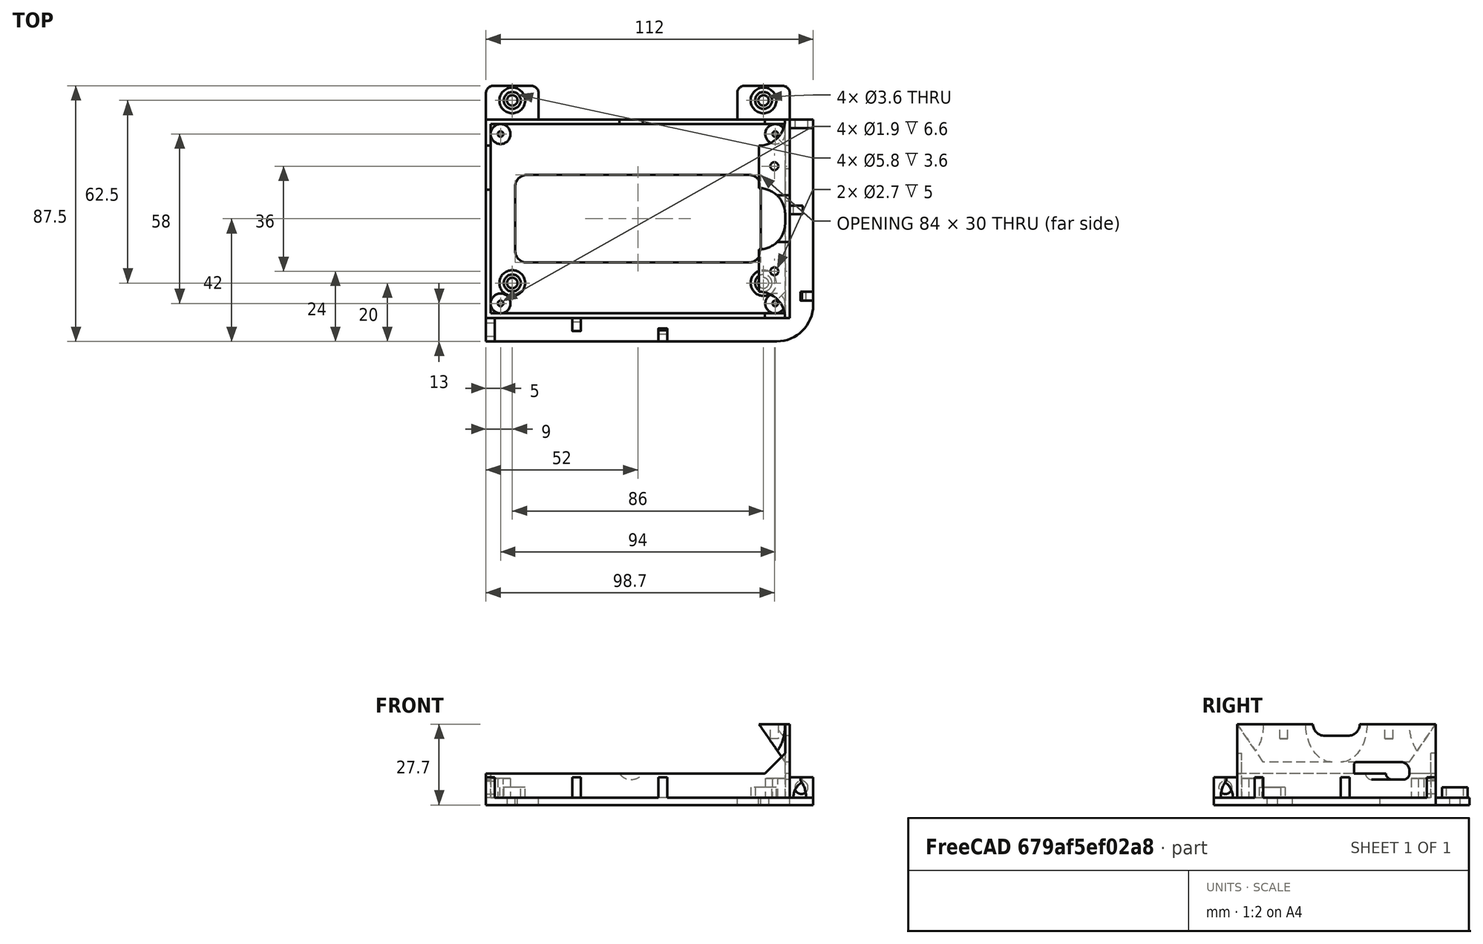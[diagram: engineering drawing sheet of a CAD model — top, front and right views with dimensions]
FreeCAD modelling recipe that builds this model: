
FCSTD DOCUMENT  (FreeCAD 1.0R39319 (Git))
Label: NanoPC-Rail-90
License: All rights reserved
LicenseURL: https://en.wikipedia.org/wiki/All_rights_reserved
objects: Sketcher::SketchObject×22, PartDesign::Pocket×13, PartDesign::Pad×9, App::VarSet×1, PartDesign::Body×1
note: 111 computed .brp shape members not serialized (recipe doc carries the construction recipe); baked Part::Feature solids carry a one-line shape summary decoded from their .brp

FEATURE [App::VarSet] VarSet
  BlackSelfTappingDiameter = 2.7
  Border = 8.2
  DX = 104
  DY = 68
  HoleDX = 94
  HoleDY = 58
  M3HeadDiameter = 5.8
  M3PassThroughDiameter = 3.6
  MiniBlackSelfTappingDiameter = 1.9
  PcbDX = 100.8
  PcbDY = 64.8
  PoleDiameter = 6.8
  PoleHeight = 6.6
  RailScrewDistance = 62.5
  Thickness = 2.5
  TopPcbWallHeight = 17
  WallThickness = 1.6
  expr: DX = PcbDX + 2 * WallThickness
  expr: DY = PcbDY + 2 * WallThickness
FEATURE [Sketcher::SketchObject] Sketch
  ArcFitTolerance = 1e-06
  AttachmentSupport = -> [XY_Plane]
  FullyConstrained = true
  MakeInternals = false
  MapMode = 5
  expr: Constraints[10] = VarSet.DY
  expr: Constraints[55] = VarSet.M3PassThroughDiameter
  expr: Constraints[64] = VarSet.RailScrewDistance
  expr: Constraints[9] = VarSet.DX
  sketch-geometry (46):
    g0: LineSegment StartX=-52 StartY=34 StartZ=0 EndX=-52 EndY=-34 EndZ=0
    g1: LineSegment [constr] StartX=-52 StartY=-34 StartZ=0 EndX=52 EndY=-34 EndZ=0
    g2: LineSegment [constr] StartX=52 StartY=-34 StartZ=0 EndX=52 EndY=34 EndZ=0
    g3: LineSegment [constr] StartX=52 StartY=34 StartZ=0 EndX=-52 EndY=34 EndZ=0
    g4: LineSegment StartX=-52 StartY=-34 StartZ=0 EndX=-52 EndY=-42 EndZ=0
    g5: LineSegment StartX=-52 StartY=-42 StartZ=0 EndX=47.5 EndY=-42 EndZ=0
    g6: LineSegment StartX=52 StartY=34 StartZ=0 EndX=60 EndY=34 EndZ=0
    g7: LineSegment StartX=60 StartY=34 StartZ=0 EndX=60 EndY=-29.5 EndZ=0
    g8: LineSegment StartX=-42 StartY=11 StartZ=0 EndX=-42 EndY=-11 EndZ=0
    g9: LineSegment StartX=-38 StartY=-15 StartZ=0 EndX=38 EndY=-15 EndZ=0
    g10: LineSegment StartX=42 StartY=-11 StartZ=0 EndX=42 EndY=11 EndZ=0
    g11: LineSegment StartX=38 StartY=15 StartZ=0 EndX=-38 EndY=15 EndZ=0
    g12: ArcOfCircle CenterX=-38 CenterY=11 CenterZ=0 NormalX=0 NormalY=0 NormalZ=1 AngleXU=0 Radius=4 StartAngle=1.5708 EndAngle=3.14159
    g13: ArcOfCircle CenterX=-38 CenterY=-11 CenterZ=0 NormalX=0 NormalY=0 NormalZ=1 AngleXU=0 Radius=4 StartAngle=3.14159 EndAngle=4.71239
    g14: ArcOfCircle CenterX=38 CenterY=-11 CenterZ=0 NormalX=0 NormalY=0 NormalZ=1 AngleXU=0 Radius=4 StartAngle=4.71239 EndAngle=6.28319
    g15: ArcOfCircle CenterX=38 CenterY=11 CenterZ=0 NormalX=0 NormalY=0 NormalZ=1 AngleXU=0 Radius=4 StartAngle=0 EndAngle=1.5708
    g16: GeomPoint [constr] X=-42 Y=15 Z=0
    g17: GeomPoint [constr] X=42 Y=-15 Z=0
    g18: LineSegment [constr] StartX=-42 StartY=11 StartZ=0 EndX=-52 EndY=11 EndZ=0
    g19: LineSegment [constr] StartX=-38 StartY=15 StartZ=0 EndX=-38 EndY=34 EndZ=0
    g20: ArcOfCircle CenterX=47.5 CenterY=-29.5 CenterZ=0 NormalX=0 NormalY=0 NormalZ=1 AngleXU=0 Radius=12.5 StartAngle=4.71239 EndAngle=6.28319
    g21: Circle CenterX=-43 CenterY=-22 CenterZ=0 NormalX=0 NormalY=0 NormalZ=1 AngleXU=0 Radius=1.8
    g22: Circle CenterX=43 CenterY=-22 CenterZ=0 NormalX=0 NormalY=0 NormalZ=1 AngleXU=0 Radius=1.8
    g23: LineSegment [constr] StartX=-43 StartY=-22 StartZ=0 EndX=-52 EndY=-22 EndZ=0
    g24: Circle CenterX=-43 CenterY=40.5 CenterZ=0 NormalX=0 NormalY=0 NormalZ=1 AngleXU=0 Radius=1.8
    g25: LineSegment [constr] StartX=-43 StartY=-22 StartZ=0 EndX=-43 EndY=40.5 EndZ=0
    g26: LineSegment [constr] StartX=43 StartY=-22 StartZ=0 EndX=43 EndY=-34 EndZ=0
    g27: LineSegment [constr] StartX=43 StartY=-22 StartZ=0 EndX=43 EndY=40.5 EndZ=0
    g28: Circle CenterX=43 CenterY=40.5 CenterZ=0 NormalX=0 NormalY=0 NormalZ=1 AngleXU=0 Radius=1.8
    g29: LineSegment StartX=-52 StartY=34 StartZ=0 EndX=-52 EndY=43 EndZ=0
    g30: LineSegment StartX=-34 StartY=34 StartZ=0 EndX=-34 EndY=43 EndZ=0
    g31: LineSegment StartX=-49.5 StartY=45.5 StartZ=0 EndX=-36.5 EndY=45.5 EndZ=0
    g32: ArcOfCircle CenterX=-36.5 CenterY=43 CenterZ=0 NormalX=0 NormalY=0 NormalZ=1 AngleXU=0 Radius=2.5 StartAngle=0 EndAngle=1.5708
    g33: ArcOfCircle CenterX=-49.5 CenterY=43 CenterZ=0 NormalX=0 NormalY=0 NormalZ=1 AngleXU=0 Radius=2.5 StartAngle=1.5708 EndAngle=3.14159
    g34: LineSegment [constr] StartX=-52 StartY=34 StartZ=0 EndX=-43 EndY=40.5 EndZ=0
    g35: LineSegment [constr] StartX=-34 StartY=34 StartZ=0 EndX=-43 EndY=40.5 EndZ=0
    g36: LineSegment [constr] StartX=-43 StartY=40.5 StartZ=0 EndX=-43 EndY=45.5 EndZ=0
    g37: LineSegment [constr] StartX=43 StartY=40.5 StartZ=0 EndX=34 EndY=34 EndZ=0
    g38: LineSegment [constr] StartX=43 StartY=40.5 StartZ=0 EndX=52 EndY=34 EndZ=0
    g39: LineSegment StartX=34 StartY=34 StartZ=0 EndX=34 EndY=43 EndZ=0
    g40: LineSegment StartX=52 StartY=34 StartZ=0 EndX=52 EndY=43 EndZ=0
    g41: LineSegment [constr] StartX=43 StartY=40.5 StartZ=0 EndX=43 EndY=45.5 EndZ=0
    g42: LineSegment StartX=36.5 StartY=45.5 StartZ=0 EndX=49.5 EndY=45.5 EndZ=0
    g43: ArcOfCircle CenterX=49.5 CenterY=43 CenterZ=0 NormalX=0 NormalY=0 NormalZ=1 AngleXU=0 Radius=2.5 StartAngle=1e-16 EndAngle=1.5708
    g44: ArcOfCircle CenterX=36.5 CenterY=43 CenterZ=0 NormalX=0 NormalY=0 NormalZ=1 AngleXU=0 Radius=2.5 StartAngle=1.5708 EndAngle=3.14159
    g45: LineSegment StartX=-34 StartY=34 StartZ=0 EndX=34 EndY=34 EndZ=0
  constraints (117):
    c: Coincident(g0,g1)
    c: Coincident(g1,g2)
    c: Coincident(g2,g3)
    c: Coincident(g3,g0)
    c: Vertical(g0)
    c: Vertical(g2)
    c: Horizontal(g1)
    c: Horizontal(g3)
    c: Symmetric(g1,g0,g-1)
    c: Distance(g3) = 104
    c: Distance(g2) = 68
    c: Coincident(g4,g0)
    c: Vertical(g4)
    c: Coincident(g5,g4)
    c: Horizontal(g5)
    c: Coincident(g6,g2)
    c: Horizontal(g6)
    c: Coincident(g7,g6)
    c: Vertical(g7)
    c: Equal(g6,g4)
    c: Distance(g4) = 8
    c: Tangent(g8,g12) = -1.5708
    c: Tangent(g8,g13) = -1.5708
    c: Tangent(g9,g13) = -1.5708
    c: Tangent(g9,g14) = -1.5708
    c: Tangent(g10,g14) = -1.5708
    c: Tangent(g10,g15) = -1.5708
    c: Tangent(g11,g15) = -1.5708
    c: Tangent(g11,g12) = -1.5708
    c: Vertical(g8)
    c: Vertical(g10)
    c: Horizontal(g9)
    c: Horizontal(g11)
    c: Equal(g12,g13)
    c: Equal(g13,g14)
    c: Equal(g14,g15)
    c: PointOnObject(g16,g8)
    c: PointOnObject(g16,g11)
    c: PointOnObject(g17,g9)
    c: PointOnObject(g17,g10)
    c: Diameter(g15) = 8
    c: Symmetric(g16,g17,g-1)
    c: Coincident(g18,g8)
    c: PointOnObject(g18,g0)
    c: Horizontal(g18)
    c: Distance(g18) = 10
    c: Coincident(g19,g11)
    c: PointOnObject(g19,g3)
    c: Vertical(g19)
    c: Distance(g19) = 19
    c: Diameter(g20) = 25
    c: Tangent(g7,g20) = 1.5708
    c: Tangent(g5,g20) = -1.5708
    c: Symmetric(g22,g21,g-2)
    c: Equal(g22,g21)
    c: Diameter(g22) = 3.6
    c: Coincident(g23,g21)
    c: Horizontal(g23)
    c: PointOnObject(g23,g0)
    c: Distance(g23) = 9
    c: Equal(g24,g22)
    c: Coincident(g25,g21)
    c: Vertical(g25)
    c: Coincident(g25,g24)
    c: Distance(g25) = 62.5
    c: Coincident(g26,g22)
    c: Vertical(g26)
    c: PointOnObject(g26,g1)
    c: Coincident(g27,g22)
    c: Vertical(g27)
    c: Equal(g25,g27)
    c: Coincident(g28,g27)
    c: Equal(g22,g28)
    c: Coincident(g29,g0)
    c: Vertical(g29)
    c: PointOnObject(g30,g3)
    c: Vertical(g30)
    c: Horizontal(g31)
    c: Equal(g29,g30)
    c: Tangent(g33,g31) = 1.5708
    c: Tangent(g33,g29) = 1.5708
    c: Coincident(g32,g30)
    c: Equal(g32,g33)
    c: Coincident(g34,g0)
    c: Coincident(g34,g24)
    c: Coincident(g35,g30)
    c: Coincident(g35,g24)
    c: Equal(g34,g35)
    c: Tangent(g32,g31) = 1.5708
    c: Coincident(g36,g24)
    c: Symmetric(g31,g31,g36)
    c: Distance(g36) = 5
    c: Diameter(g32) = 5
    c: Coincident(g37,g27)
    c: PointOnObject(g37,g3)
    c: Equal(g35,g37)
    c: Coincident(g38,g27)
    c: PointOnObject(g38,g3)
    c: Equal(g37,g38)
    c: Coincident(g39,g37)
    c: Vertical(g39)
    c: Coincident(g40,g38)
    c: Vertical(g40)
    c: Coincident(g41,g27)
    c: Vertical(g41)
    c: Equal(g41,g36)
    c: Horizontal(g42)
    c: PointOnObject(g41,g42)
    c: Tangent(g44,g42) = 1.5708
    c: Tangent(g43,g42) = 1.5708
    c: Tangent(g43,g40) = -1.5708
    c: Tangent(g44,g39) = 1.5708
    c: Equal(g32,g44)
    c: Equal(g44,g43)
    c: Coincident(g45,g30)
    c: Coincident(g45,g37)
    c: Distance(g26) = 12
FEATURE [PartDesign::Pad] Pad  label="Base Structure"
  Direction = (0,0,1)
  Length = 2.5
  Length2 = 10
  Profile = -> Sketch
  ReferenceAxis = -> Sketch [N_Axis]
  Refine = true
  Suppressed = false
  Type = 0
  expr: Length = VarSet.Thickness
FEATURE [Sketcher::SketchObject] Sketch002
  ArcFitTolerance = 1e-06
  AttachmentSupport = -> [Pad]
  FullyConstrained = true
  MakeInternals = false
  MapMode = 5
  Placement = pos=(0,0,2.5) rot=(0,0,1;0rad)
  expr: Constraints[10] = VarSet.PcbDX
  expr: Constraints[17] = VarSet.DX
  expr: Constraints[20] = VarSet.DY
  expr: Constraints[9] = VarSet.PcbDY
  sketch-geometry (8):
    g0: LineSegment StartX=-50.4 StartY=32.4 StartZ=0 EndX=-50.4 EndY=-32.4 EndZ=0
    g1: LineSegment StartX=-50.4 StartY=-32.4 StartZ=0 EndX=50.4 EndY=-32.4 EndZ=0
    g2: LineSegment StartX=50.4 StartY=-32.4 StartZ=0 EndX=50.4 EndY=32.4 EndZ=0
    g3: LineSegment StartX=50.4 StartY=32.4 StartZ=0 EndX=-50.4 EndY=32.4 EndZ=0
    g4: LineSegment StartX=-52 StartY=34 StartZ=0 EndX=-52 EndY=-34 EndZ=0
    g5: LineSegment StartX=-52 StartY=-34 StartZ=0 EndX=52 EndY=-34 EndZ=0
    g6: LineSegment StartX=52 StartY=-34 StartZ=0 EndX=52 EndY=34 EndZ=0
    g7: LineSegment StartX=52 StartY=34 StartZ=0 EndX=-52 EndY=34 EndZ=0
  constraints (21):
    c: Coincident(g0,g1)
    c: Coincident(g1,g2)
    c: Coincident(g2,g3)
    c: Coincident(g3,g0)
    c: Vertical(g0)
    c: Vertical(g2)
    c: Horizontal(g1)
    c: Horizontal(g3)
    c: Symmetric(g1,g0,g-1)
    c: Distance(g2) = 64.8
    c: Distance(g3) = 100.8
    c: Coincident(g4,g5)
    c: Coincident(g5,g6)
    c: Coincident(g6,g7)
    c: Coincident(g7,g4)
    c: Horizontal(g5)
    c: Symmetric(g6,g4,g-2)
    c: Distance(g7) = 104
    c: Equal(g5,g7)
    c: Symmetric(g5,g6,g-1)
    c: Distance(g6) = 68
FEATURE [PartDesign::Pad] Pad001  label="Border"
  BaseFeature = -> Pad
  Direction = (0,0,1)
  Length = 8.2
  Length2 = 10
  Profile = -> Sketch002
  ReferenceAxis = -> Sketch002 [N_Axis]
  Refine = true
  Suppressed = false
  Type = 0
  expr: Length = VarSet.Border
FEATURE [Sketcher::SketchObject] Sketch003
  ArcFitTolerance = 1e-06
  AttachmentSupport = -> [Pad001]
  FullyConstrained = true
  MakeInternals = false
  MapMode = 5
  Placement = pos=(0,0,2.5) rot=(0,0,1;0rad)
  expr: Constraints[12] = VarSet.PoleDiameter
  expr: Constraints[20] = VarSet.MiniBlackSelfTappingDiameter
  expr: Constraints[5] = VarSet.HoleDX
  expr: Constraints[6] = VarSet.HoleDY
  sketch-geometry (10):
    g0: Circle CenterX=-47 CenterY=29 CenterZ=0 NormalX=0 NormalY=0 NormalZ=1 AngleXU=0 Radius=3.4
    g1: Circle CenterX=47 CenterY=29 CenterZ=0 NormalX=0 NormalY=0 NormalZ=1 AngleXU=0 Radius=3.4
    g2: Circle CenterX=47 CenterY=-29 CenterZ=0 NormalX=0 NormalY=0 NormalZ=1 AngleXU=0 Radius=3.4
    g3: Circle CenterX=-47 CenterY=-29 CenterZ=0 NormalX=0 NormalY=0 NormalZ=1 AngleXU=0 Radius=3.4
    g4: LineSegment [constr] StartX=-47 StartY=29 StartZ=0 EndX=47 EndY=29 EndZ=0
    g5: LineSegment [constr] StartX=47 StartY=29 StartZ=0 EndX=47 EndY=-29 EndZ=0
    g6: Circle CenterX=-47 CenterY=29 CenterZ=0 NormalX=0 NormalY=0 NormalZ=1 AngleXU=0 Radius=0.95
    g7: Circle CenterX=47 CenterY=29 CenterZ=0 NormalX=0 NormalY=0 NormalZ=1 AngleXU=0 Radius=0.95
    g8: Circle CenterX=47 CenterY=-29 CenterZ=0 NormalX=0 NormalY=0 NormalZ=1 AngleXU=0 Radius=0.95
    g9: Circle CenterX=-47 CenterY=-29 CenterZ=0 NormalX=0 NormalY=0 NormalZ=1 AngleXU=0 Radius=0.95
  constraints (21):
    c: Coincident(g4,g0)
    c: Coincident(g5,g1)
    c: Coincident(g5,g2)
    c: Coincident(g4,g1)
    c: Symmetric(g1,g0,g-2)
    c: Distance(g4) = 94
    c: Distance(g5) = 58
    c: Symmetric(g2,g1,g-1)
    c: Symmetric(g3,g2,g-2)
    c: Equal(g1,g2)
    c: Equal(g2,g3)
    c: Equal(g3,g0)
    c: Diameter(g3) = 6.8
    c: Coincident(g6,g0)
    c: Coincident(g7,g1)
    c: Coincident(g8,g2)
    c: Coincident(g9,g3)
    c: Equal(g9,g6)
    c: Equal(g6,g8)
    c: Equal(g8,g7)
    c: Diameter(g6) = 1.9
FEATURE [PartDesign::Pad] Pad002  label="Screw Poles"
  BaseFeature = -> Pad001
  Direction = (0,0,1)
  Length = 6.6
  Length2 = 10
  Profile = -> Sketch003
  ReferenceAxis = -> Sketch003 [N_Axis]
  Refine = true
  Suppressed = false
  Type = 0
  expr: Length = VarSet.PoleHeight
FEATURE [Sketcher::SketchObject] Sketch004
  ArcFitTolerance = 1e-06
  AttachmentSupport = -> [Pad002]
  ExternalGeometry = -> [Pad002]
  FullyConstrained = true
  MakeInternals = false
  MapMode = 5
  Placement = pos=(0,0,2.5) rot=(0,0,1;0rad)
  sketch-geometry (36):
    g0: LineSegment [constr] StartX=-52 StartY=-34 StartZ=0 EndX=-52 EndY=-42 EndZ=0
    g1: LineSegment [constr] StartX=-52 StartY=-42 StartZ=0 EndX=10 EndY=-42 EndZ=0
    g2: LineSegment [constr] StartX=10 StartY=-42 StartZ=0 EndX=10 EndY=-34 EndZ=0
    g3: LineSegment [constr] StartX=10 StartY=-34 StartZ=0 EndX=-52 EndY=-34 EndZ=0
    g4: LineSegment [constr] StartX=52 StartY=34 StartZ=0 EndX=52 EndY=-28 EndZ=0
    g5: LineSegment [constr] StartX=52 StartY=-28 StartZ=0 EndX=60 EndY=-28 EndZ=0
    g6: LineSegment [constr] StartX=60 StartY=-28 StartZ=0 EndX=60 EndY=34 EndZ=0
    g7: LineSegment [constr] StartX=60 StartY=34 StartZ=0 EndX=52 EndY=34 EndZ=0
    g8: LineSegment StartX=-52 StartY=-34 StartZ=0 EndX=-52 EndY=-42 EndZ=0
    g9: LineSegment StartX=-52 StartY=-42 StartZ=0 EndX=-49 EndY=-42 EndZ=0
    g10: LineSegment StartX=-49 StartY=-42 StartZ=0 EndX=-49 EndY=-34 EndZ=0
    g11: LineSegment StartX=-49 StartY=-34 StartZ=0 EndX=-52 EndY=-34 EndZ=0
    g12: LineSegment StartX=-22.5 StartY=-34 StartZ=0 EndX=-22.5 EndY=-38.4 EndZ=0
    g13: LineSegment StartX=-22.5 StartY=-38.4 StartZ=0 EndX=-19.5 EndY=-38.4 EndZ=0
    g14: LineSegment StartX=-19.5 StartY=-38.4 StartZ=0 EndX=-19.5 EndY=-34 EndZ=0
    g15: LineSegment StartX=-19.5 StartY=-34 StartZ=0 EndX=-22.5 EndY=-34 EndZ=0
    g16: LineSegment StartX=10 StartY=-42 StartZ=0 EndX=10 EndY=-37.6 EndZ=0
    g17: LineSegment StartX=10 StartY=-37.6 StartZ=0 EndX=7 EndY=-37.6 EndZ=0
    g18: LineSegment StartX=7 StartY=-37.6 StartZ=0 EndX=7 EndY=-42 EndZ=0
    g19: LineSegment StartX=7 StartY=-42 StartZ=0 EndX=10 EndY=-42 EndZ=0
    g20: LineSegment StartX=52 StartY=34 StartZ=0 EndX=52 EndY=31 EndZ=0
    g21: LineSegment StartX=52 StartY=31 StartZ=0 EndX=60 EndY=31 EndZ=0
    g22: LineSegment StartX=60 StartY=31 StartZ=0 EndX=60 EndY=34 EndZ=0
    g23: LineSegment StartX=60 StartY=34 StartZ=0 EndX=52 EndY=34 EndZ=0
    g24: LineSegment StartX=52 StartY=4.5 StartZ=0 EndX=52 EndY=1.5 EndZ=0
    g25: LineSegment StartX=52 StartY=1.5 StartZ=0 EndX=56.4 EndY=1.5 EndZ=0
    g26: LineSegment StartX=56.4 StartY=1.5 StartZ=0 EndX=56.4 EndY=4.5 EndZ=0
    g27: LineSegment StartX=56.4 StartY=4.5 StartZ=0 EndX=52 EndY=4.5 EndZ=0
    g28: LineSegment StartX=60 StartY=-28 StartZ=0 EndX=60 EndY=-25 EndZ=0
    g29: LineSegment StartX=60 StartY=-25 StartZ=0 EndX=55.6 EndY=-25 EndZ=0
    g30: LineSegment StartX=55.6 StartY=-25 StartZ=0 EndX=55.6 EndY=-28 EndZ=0
    g31: LineSegment StartX=55.6 StartY=-28 StartZ=0 EndX=60 EndY=-28 EndZ=0
    g32: LineSegment [constr] StartX=-52 StartY=-42 StartZ=0 EndX=-22.5 EndY=-38.4 EndZ=0
    g33: LineSegment [constr] StartX=10 StartY=-42 StartZ=0 EndX=-19.5 EndY=-38.4 EndZ=0
    g34: LineSegment [constr] StartX=56.4 StartY=1.5 StartZ=0 EndX=60 EndY=-28 EndZ=0
    g35: LineSegment [constr] StartX=56.4 StartY=4.5 StartZ=0 EndX=60 EndY=34 EndZ=0
  constraints (98):
    c: Coincident(g0,g1)
    c: Coincident(g1,g2)
    c: Coincident(g2,g3)
    c: Coincident(g3,g0)
    c: Vertical(g0)
    c: Vertical(g2)
    c: Horizontal(g1)
    c: Horizontal(g3)
    c: Coincident(g4,g5)
    c: Coincident(g5,g6)
    c: Coincident(g6,g7)
    c: Coincident(g7,g4)
    c: Vertical(g4)
    c: Vertical(g6)
    c: Horizontal(g5)
    c: Horizontal(g7)
    c: Equal(g5,g2)
    c: Distance(g7) = 8
    c: Coincident(g6,g-4)
    c: Coincident(g0,g-3)
    c: Distance(g1) = 62
    c: Equal(g1,g6)
    c: Coincident(g8,g9)
    c: Coincident(g9,g10)
    c: Coincident(g10,g11)
    c: Coincident(g11,g8)
    c: Vertical(g8)
    c: Vertical(g10)
    c: Horizontal(g9)
    c: Horizontal(g11)
    c: Coincident(g8,g0)
    c: PointOnObject(g9,g1)
    c: Distance(g9) = 3
    c: Coincident(g12,g13)
    c: Coincident(g13,g14)
    c: Coincident(g14,g15)
    c: Coincident(g15,g12)
    c: Vertical(g12)
    c: Vertical(g14)
    c: Horizontal(g13)
    c: Horizontal(g15)
    c: Equal(g9,g13)
    c: Coincident(g16,g17)
    c: Coincident(g17,g18)
    c: Coincident(g18,g19)
    c: Coincident(g19,g16)
    c: Vertical(g16)
    c: Vertical(g18)
    c: Horizontal(g17)
    c: Horizontal(g19)
    c: Coincident(g16,g1)
    c: Equal(g19,g13)
    c: Coincident(g20,g21)
    c: Coincident(g21,g22)
    c: Coincident(g22,g23)
    c: Coincident(g23,g20)
    c: Vertical(g20)
    c: Vertical(g22)
    c: Horizontal(g21)
    c: Horizontal(g23)
    c: Coincident(g20,g4)
    c: PointOnObject(g21,g6)
    c: Equal(g19,g22)
    c: Coincident(g24,g25)
    c: Coincident(g25,g26)
    c: Coincident(g26,g27)
    c: Coincident(g27,g24)
    c: Vertical(g24)
    c: Vertical(g26)
    c: Horizontal(g25)
    c: Horizontal(g27)
    c: Coincident(g28,g29)
    c: Coincident(g29,g30)
    c: Coincident(g30,g31)
    c: Coincident(g31,g28)
    c: Vertical(g28)
    c: Vertical(g30)
    c: Horizontal(g29)
    c: Horizontal(g31)
    c: Coincident(g28,g5)
    c: Equal(g28,g26)
    c: Equal(g26,g19)
    c: Distance(g12) = 4.4
    c: Distance(g27) = 4.4
    c: PointOnObject(g14,g3)
    c: Equal(g14,g18)
    c: Coincident(g32,g0)
    c: Coincident(g32,g12)
    c: Coincident(g33,g1)
    c: Coincident(g33,g13)
    c: Equal(g33,g32)
    c: PointOnObject(g24,g4)
    c: Equal(g25,g29)
    c: Coincident(g34,g25)
    c: Coincident(g34,g5)
    c: Coincident(g35,g26)
    c: Coincident(g35,g6)
    c: Equal(g34,g35)
FEATURE [Sketcher::SketchObject] Sketch015
  ArcFitTolerance = 1e-06
  AttachmentSupport = -> [Pad002]
  ExternalGeometry = -> [Pad002]
  FullyConstrained = true
  MakeInternals = false
  MapMode = 5
  Placement = pos=(0,0,2.5) rot=(0,0,1;0rad)
  expr: Constraints[11] = VarSet.M3HeadDiameter + 3 mm
  expr: Constraints[3] = VarSet.M3HeadDiameter
  sketch-geometry (8):
    g0: Circle CenterX=-43 CenterY=40.5 CenterZ=0 NormalX=0 NormalY=0 NormalZ=1 AngleXU=0 Radius=2.9
    g1: Circle CenterX=43 CenterY=40.5 CenterZ=0 NormalX=0 NormalY=0 NormalZ=1 AngleXU=0 Radius=2.9
    g2: Circle CenterX=43 CenterY=-22 CenterZ=0 NormalX=0 NormalY=0 NormalZ=1 AngleXU=0 Radius=2.9
    g3: Circle CenterX=-43 CenterY=-22 CenterZ=0 NormalX=0 NormalY=0 NormalZ=1 AngleXU=0 Radius=2.9
    g4: Circle CenterX=43 CenterY=40.5 CenterZ=0 NormalX=0 NormalY=0 NormalZ=1 AngleXU=0 Radius=4.4
    g5: Circle CenterX=43 CenterY=-22 CenterZ=0 NormalX=0 NormalY=0 NormalZ=1 AngleXU=0 Radius=4.4
    g6: Circle CenterX=-43 CenterY=-22 CenterZ=0 NormalX=0 NormalY=0 NormalZ=1 AngleXU=0 Radius=4.4
    g7: Circle CenterX=-43 CenterY=40.5 CenterZ=0 NormalX=0 NormalY=0 NormalZ=1 AngleXU=0 Radius=4.4
  constraints (16):
    c: Equal(g0,g1)
    c: Equal(g1,g2)
    c: Equal(g2,g3)
    c: Diameter(g1) = 5.8
    c: Coincident(g4,g1)
    c: Coincident(g5,g2)
    c: Coincident(g6,g3)
    c: Coincident(g7,g0)
    c: Equal(g6,g7)
    c: Equal(g7,g4)
    c: Equal(g4,g5)
    c: Diameter(g4) = 8.8
    c: Coincident(g2,g-5)
    c: Coincident(g3,g-6)
    c: Coincident(g0,g-3)
    c: Coincident(g1,g-4)
FEATURE [PartDesign::Pad] Pad004  label="Rail Clamp Screws"
  BaseFeature = -> Pad002
  Direction = (0,0,1)
  Length = 3.6
  Length2 = 10
  Profile = -> Sketch015
  ReferenceAxis = -> Sketch015 [N_Axis]
  Refine = true
  Suppressed = false
  Type = 0
FEATURE [PartDesign::Pad] Pad003  label="Antenna Holders"
  BaseFeature = -> Pad004
  Direction = (0,0,1)
  Length = 7
  Length2 = 10
  Profile = -> Sketch004
  ReferenceAxis = -> Sketch004 [N_Axis]
  Refine = true
  Suppressed = false
  Type = 0
FEATURE [Sketcher::SketchObject] Sketch005
  ArcFitTolerance = 1e-06
  AttachmentSupport = -> [Pad003]
  ExternalGeometry = -> [Pad003]
  FullyConstrained = true
  MakeInternals = false
  MapMode = 5
  Placement = pos=(-49,0,0) rot=(0.57735,0.57735,0.57735;2.0944rad)
  sketch-geometry (1):
    g0: Circle CenterX=-38 CenterY=6 CenterZ=0 NormalX=0 NormalY=0 NormalZ=1 AngleXU=0 Radius=2.25
  constraints (2):
    c: Symmetric(g-4,g-3,g0)
    c: Diameter(g0) = 4.5
FEATURE [PartDesign::Pocket] Pocket001  label="Hole 1"
  BaseFeature = -> Pad003
  Direction = (-1,0,0)
  Length = 5
  Length2 = 2
  Profile = -> Sketch005
  ReferenceAxis = -> Sketch005 [N_Axis]
  Refine = true
  Suppressed = false
  Type = 0
FEATURE [Sketcher::SketchObject] Sketch006
  ArcFitTolerance = 1e-06
  AttachmentSupport = -> [Pocket001]
  ExternalGeometry = -> [Pocket001]
  FullyConstrained = true
  MakeInternals = false
  MapMode = 5
  Placement = pos=(0,31,0) rot=(1,0,0;1.5708rad)
  sketch-geometry (1):
    g0: Circle CenterX=56 CenterY=6 CenterZ=0 NormalX=0 NormalY=0 NormalZ=1 AngleXU=0 Radius=2.25
  constraints (2):
    c: Diameter(g0) = 4.5
    c: Symmetric(g-4,g-3,g0)
FEATURE [PartDesign::Pocket] Pocket002  label="Hole 2"
  BaseFeature = -> Pocket001
  Direction = (0,1,-2e-16)
  Length = 5
  Length2 = 5
  Profile = -> Sketch006
  ReferenceAxis = -> Sketch006 [N_Axis]
  Refine = true
  Suppressed = false
  Type = 0
FEATURE [Sketcher::SketchObject] Sketch007
  ArcFitTolerance = 1e-06
  AttachmentSupport = -> [Pocket002]
  ExternalGeometry = -> [Pocket002]
  FullyConstrained = true
  MakeInternals = false
  MapMode = 5
  Placement = pos=(0,1.5,0) rot=(1,0,0;1.5708rad)
  sketch-geometry (5):
    g0: LineSegment StartX=56.4 StartY=9.5 StartZ=0 EndX=55.4 EndY=9.5 EndZ=0
    g1: LineSegment StartX=56.4 StartY=2.5 StartZ=0 EndX=53.2 EndY=2.5 EndZ=0
    g2: ArcOfCircle CenterX=55.4 CenterY=8.5 CenterZ=0 NormalX=0 NormalY=0 NormalZ=1 AngleXU=0 Radius=1 StartAngle=5.30327 EndAngle=7.85398
    g3: LineSegment StartX=56.4 StartY=9.5 StartZ=0 EndX=56.4 EndY=2.5 EndZ=0
    g4: ArcOfCircle CenterX=59.425 CenterY=2.5 CenterZ=0 NormalX=0 NormalY=0 NormalZ=1 AngleXU=0 Radius=6.225 StartAngle=2.16168 EndAngle=3.14159
  constraints (14):
    c: Coincident(g0,g-3)
    c: Horizontal(g0)
    c: Coincident(g1,g-3)
    c: Horizontal(g1)
    c: Distance(g0) = 1
    c: Distance(g1) = 3.2
    c: Coincident(g2,g0)
    c: Diameter(g2) = 2
    c: Tangent(g2,g-3)
    c: Coincident(g3,g0)
    c: Coincident(g3,g1)
    c: Coincident(g4,g1)
    c: Perpendicular(g4,g1)
    c: Tangent(g4,g2) = 1.5708
FEATURE [PartDesign::Pocket] Pocket003  label="Hook 1"
  BaseFeature = -> Pocket002
  Direction = (0,1,-2e-16)
  Length = 5
  Length2 = 5
  Profile = -> Sketch007
  ReferenceAxis = -> Sketch007 [N_Axis]
  Refine = true
  Suppressed = false
  Type = 0
FEATURE [Sketcher::SketchObject] Sketch008
  ArcFitTolerance = 1e-06
  AttachmentSupport = -> [Pocket003]
  ExternalGeometry = -> [Pocket003]
  FullyConstrained = true
  MakeInternals = false
  MapMode = 5
  Placement = pos=(0,-28,0) rot=(1,0,0;1.5708rad)
  sketch-geometry (5):
    g0: LineSegment StartX=55.6 StartY=9.5 StartZ=0 EndX=56.6 EndY=9.5 EndZ=0
    g1: LineSegment StartX=55.6 StartY=2.5 StartZ=0 EndX=57.6 EndY=2.5 EndZ=0
    g2: ArcOfCircle CenterX=56.4 CenterY=8.7254 CenterZ=0 NormalX=0 NormalY=0 NormalZ=1 AngleXU=0 Radius=0.8 StartAngle=1.31812 EndAngle=3.76329
    g3: ArcOfCircle CenterX=47.7111 CenterY=2.5 CenterZ=0 NormalX=0 NormalY=0 NormalZ=1 AngleXU=0 Radius=9.88891 StartAngle=-9e-16 EndAngle=0.621699
    g4: LineSegment StartX=55.6 StartY=9.5 StartZ=0 EndX=55.6 EndY=2.5 EndZ=0
  constraints (14):
    c: Coincident(g0,g-3)
    c: Horizontal(g0)
    c: Coincident(g1,g-3)
    c: Horizontal(g1)
    c: Distance(g0) = 1
    c: Distance(g1) = 2
    c: Coincident(g2,g0)
    c: Diameter(g2) = 1.6
    c: Tangent(g-3,g2)
    c: Coincident(g3,g1)
    c: Perpendicular(g3,g1)
    c: Tangent(g3,g2) = 1.5708
    c: Coincident(g4,g0)
    c: Coincident(g4,g1)
FEATURE [PartDesign::Pocket] Pocket004  label="Hook 2"
  BaseFeature = -> Pocket003
  Direction = (0,1,-2e-16)
  Length = 5
  Length2 = 5
  Profile = -> Sketch008
  ReferenceAxis = -> Sketch008 [N_Axis]
  Refine = true
  Suppressed = false
  Type = 0
FEATURE [Sketcher::SketchObject] Sketch009
  ArcFitTolerance = 1e-06
  AttachmentSupport = -> [Pocket004]
  ExternalGeometry = -> [Pocket004]
  FullyConstrained = true
  MakeInternals = false
  MapMode = 5
  Placement = pos=(10,0,0) rot=(0.57735,0.57735,0.57735;2.0944rad)
  sketch-geometry (5):
    g0: LineSegment StartX=-37.6 StartY=9.5 StartZ=0 EndX=-38.6 EndY=9.5 EndZ=0
    g1: LineSegment StartX=-37.6 StartY=2.5 StartZ=0 EndX=-39.6 EndY=2.5 EndZ=0
    g2: ArcOfCircle CenterX=-38.4 CenterY=8.7254 CenterZ=0 NormalX=0 NormalY=0 NormalZ=1 AngleXU=0 Radius=0.8 StartAngle=5.66149 EndAngle=8.10666
    g3: ArcOfCircle CenterX=-29.7111 CenterY=2.5 CenterZ=0 NormalX=0 NormalY=0 NormalZ=1 AngleXU=0 Radius=9.88891 StartAngle=2.51989 EndAngle=3.14159
    g4: LineSegment StartX=-37.6 StartY=9.5 StartZ=0 EndX=-37.6 EndY=2.5 EndZ=0
  constraints (14):
    c: Coincident(g0,g-3)
    c: Horizontal(g0)
    c: Coincident(g1,g-3)
    c: Horizontal(g1)
    c: Distance(g1) = 2
    c: Distance(g0) = 1
    c: Coincident(g2,g0)
    c: Diameter(g2) = 1.6
    c: Tangent(g2,g-3)
    c: Coincident(g3,g1)
    c: Perpendicular(g3,g1)
    c: Tangent(g3,g2) = 1.5708
    c: Coincident(g4,g0)
    c: Coincident(g4,g1)
FEATURE [PartDesign::Pocket] Pocket005  label="Hook 3"
  BaseFeature = -> Pocket004
  Direction = (-1,0,0)
  Length = 5
  Length2 = 5
  Profile = -> Sketch009
  ReferenceAxis = -> Sketch009 [N_Axis]
  Refine = true
  Suppressed = false
  Type = 0
FEATURE [Sketcher::SketchObject] Sketch010
  ArcFitTolerance = 1e-06
  AttachmentSupport = -> [Pocket005]
  ExternalGeometry = -> [Pocket005]
  FullyConstrained = true
  MakeInternals = false
  MapMode = 5
  Placement = pos=(-19.5,0,0) rot=(0.57735,0.57735,0.57735;2.0944rad)
  sketch-geometry (5):
    g0: LineSegment StartX=-38.4 StartY=9.5 StartZ=0 EndX=-37.4 EndY=9.5 EndZ=0
    g1: LineSegment StartX=-38.4 StartY=2.5 StartZ=0 EndX=-35.4 EndY=2.5 EndZ=0
    g2: ArcOfCircle CenterX=-37.4 CenterY=8.5 CenterZ=0 NormalX=0 NormalY=0 NormalZ=1 AngleXU=0 Radius=1 StartAngle=1.5708 EndAngle=4.06889
    g3: ArcOfCircle CenterX=-41.9 CenterY=2.5 CenterZ=0 NormalX=0 NormalY=0 NormalZ=1 AngleXU=0 Radius=6.5 StartAngle=0 EndAngle=0.927295
    g4: LineSegment StartX=-38.4 StartY=9.5 StartZ=0 EndX=-38.4 EndY=2.5 EndZ=0
  constraints (14):
    c: Coincident(g0,g-3)
    c: Horizontal(g0)
    c: Coincident(g1,g-3)
    c: Horizontal(g1)
    c: Distance(g0) = 1
    c: Distance(g1) = 3
    c: Coincident(g2,g0)
    c: Diameter(g2) = 2
    c: Tangent(g2,g-3)
    c: Coincident(g3,g1)
    c: Perpendicular(g3,g1)
    c: Tangent(g3,g2) = 1.5708
    c: Coincident(g4,g0)
    c: Coincident(g4,g1)
FEATURE [PartDesign::Pocket] Pocket006  label="Hook 4"
  BaseFeature = -> Pocket005
  Direction = (-1,0,0)
  Length = 5
  Length2 = 5
  Profile = -> Sketch010
  ReferenceAxis = -> Sketch010 [N_Axis]
  Refine = true
  Suppressed = false
  Type = 0
FEATURE [Sketcher::SketchObject] Sketch012
  ArcFitTolerance = 1e-06
  AttachmentSupport = -> [Pocket006]
  FullyConstrained = true
  MakeInternals = false
  MapMode = 5
  Placement = pos=(0,34,0) rot=(0,0.707107,0.707107;3.14159rad)
  expr: Constraints[11] = VarSet.Border + VarSet.Thickness + 3 mm
  sketch-geometry (5):
    g0: Circle CenterX=2.3 CenterY=13.7 CenterZ=0 NormalX=0 NormalY=0 NormalZ=1 AngleXU=0 Radius=5
    g1: LineSegment [constr] StartX=0 StartY=0 StartZ=0 EndX=2.3 EndY=0 EndZ=0
    g2: LineSegment [constr] StartX=2.3 StartY=0 StartZ=0 EndX=2.3 EndY=13.7 EndZ=0
    g3: LineSegment [constr] StartX=2.3 StartY=13.7 StartZ=0 EndX=0 EndY=13.7 EndZ=0
    g4: LineSegment [constr] StartX=0 StartY=13.7 StartZ=0 EndX=0 EndY=0 EndZ=0
  constraints (13):
    c: Diameter(g0) = 10
    c: Coincident(g1,g2)
    c: Coincident(g2,g3)
    c: Coincident(g3,g4)
    c: Coincident(g4,g1)
    c: Horizontal(g1)
    c: Horizontal(g3)
    c: Vertical(g2)
    c: Vertical(g4)
    c: Coincident(g1,g-1)
    c: Distance(g1) = 2.3
    c: Distance(g4) = 13.7
    c: Coincident(g0,g2)
FEATURE [PartDesign::Pocket] Pocket008  label="Audio Jack"
  BaseFeature = -> Pocket006
  Direction = (0,-1,2e-16)
  Length = 5
  Length2 = 5
  Profile = -> Sketch012
  ReferenceAxis = -> Sketch012 [N_Axis]
  Refine = true
  Suppressed = false
  Type = 0
FEATURE [Sketcher::SketchObject] Sketch013
  ArcFitTolerance = 1e-06
  AttachmentSupport = -> [Pocket008]
  ExternalGeometry = -> [Pocket008]
  FullyConstrained = true
  MakeInternals = false
  MapMode = 5
  Placement = pos=(-52,0,0) rot=(0.57735,-0.57735,-0.57735;2.0944rad)
  sketch-geometry (5):
    g0: LineSegment [constr] StartX=-34 StartY=10.7 StartZ=0 EndX=-25 EndY=10.7 EndZ=0
    g1: LineSegment StartX=-25 StartY=10.7 StartZ=0 EndX=-10 EndY=10.7 EndZ=0
    g2: ArcOfCircle CenterX=-23 CenterY=10.7 CenterZ=0 NormalX=0 NormalY=0 NormalZ=1 AngleXU=0 Radius=2 StartAngle=3.14159 EndAngle=4.71239
    g3: ArcOfCircle CenterX=-12 CenterY=10.7 CenterZ=0 NormalX=0 NormalY=0 NormalZ=1 AngleXU=0 Radius=2 StartAngle=4.71239 EndAngle=6.28319
    g4: LineSegment StartX=-23 StartY=8.7 StartZ=0 EndX=-12 EndY=8.7 EndZ=0
  constraints (14):
    c: Horizontal(g0)
    c: Distance(g0) = 9
    c: Coincident(g1,g0)
    c: Horizontal(g1)
    c: Distance(g1) = 15
    c: Coincident(g2,g0)
    c: Coincident(g3,g1)
    c: Perpendicular(g3,g1)
    c: Perpendicular(g2,g1)
    c: Horizontal(g4)
    c: Tangent(g4,g2) = -1.5708
    c: Tangent(g4,g3) = -1.5708
    c: Diameter(g2) = 4
    c: Coincident(g0,g-3)
FEATURE [PartDesign::Pocket] Pocket009  label="Buttons"
  BaseFeature = -> Pocket008
  Direction = (1,0,0)
  Length = 3
  Length2 = 5
  Profile = -> Sketch013
  ReferenceAxis = -> Sketch013 [N_Axis]
  Refine = true
  Suppressed = false
  Type = 0
FEATURE [Sketcher::SketchObject] Sketch014
  ArcFitTolerance = 1e-06
  AttachmentSupport = -> [Pocket009]
  ExternalGeometry = -> [Pocket009]
  FullyConstrained = true
  MakeInternals = false
  MapMode = 5
  Placement = pos=(52,0,0) rot=(0.57735,0.57735,0.57735;2.0944rad)
  sketch-geometry (5):
    g0: LineSegment [constr] StartX=34 StartY=10.7 StartZ=0 EndX=25 EndY=10.7 EndZ=0
    g1: LineSegment StartX=25 StartY=10.7 StartZ=0 EndX=17 EndY=10.7 EndZ=0
    g2: ArcOfCircle CenterX=19 CenterY=10.7 CenterZ=0 NormalX=0 NormalY=0 NormalZ=1 AngleXU=0 Radius=2 StartAngle=3.14159 EndAngle=4.71239
    g3: ArcOfCircle CenterX=23 CenterY=10.7 CenterZ=0 NormalX=0 NormalY=0 NormalZ=1 AngleXU=0 Radius=2 StartAngle=4.71239 EndAngle=6.28319
    g4: LineSegment StartX=19 StartY=8.7 StartZ=0 EndX=23 EndY=8.7 EndZ=0
  constraints (14):
    c: Coincident(g0,g-3)
    c: PointOnObject(g0,g-3)
    c: Distance(g0) = 9
    c: Coincident(g1,g0)
    c: PointOnObject(g1,g-3)
    c: Distance(g1) = 8
    c: PointOnObject(g2,g1)
    c: Coincident(g2,g1)
    c: PointOnObject(g3,g1)
    c: Coincident(g3,g0)
    c: Diameter(g2) = 4
    c: Horizontal(g4)
    c: Tangent(g4,g2) = -1.5708
    c: Tangent(g3,g4) = -1.5708
FEATURE [PartDesign::Pocket] Pocket010  label="Reset"
  BaseFeature = -> Pocket009
  Direction = (-1,0,0)
  Length = 3
  Length2 = 5
  Profile = -> Sketch014
  ReferenceAxis = -> Sketch014 [N_Axis]
  Refine = true
  Suppressed = false
  Type = 0
FEATURE [Sketcher::SketchObject] Sketch016
  ArcFitTolerance = 1e-06
  AttachmentSupport = -> [Pocket010]
  ExternalGeometry = -> [Pocket010]
  FullyConstrained = true
  MakeInternals = false
  MapMode = 5
  Placement = pos=(52,0,0) rot=(0.57735,0.57735,0.57735;2.0944rad)
  expr: Constraints[2] = VarSet.TopPcbWallHeight
  sketch-geometry (12):
    g0: LineSegment StartX=-34 StartY=10.7 StartZ=0 EndX=-34 EndY=27.7 EndZ=0
    g1: LineSegment StartX=-34 StartY=27.7 StartZ=0 EndX=34 EndY=27.7 EndZ=0
    g2: LineSegment StartX=34 StartY=10.7 StartZ=0 EndX=34 EndY=27.7 EndZ=0
    g3: LineSegment [constr] StartX=17 StartY=10.7 StartZ=0 EndX=6 EndY=10.7 EndZ=0
    g4: LineSegment StartX=-34 StartY=10.7 StartZ=0 EndX=6 EndY=10.7 EndZ=0
    g5: LineSegment StartX=6 StartY=10.7 StartZ=0 EndX=6 EndY=13.7 EndZ=0
    g6: LineSegment StartX=7 StartY=14.7 StartZ=0 EndX=22 EndY=14.7 EndZ=0
    g7: LineSegment [constr] StartX=17 StartY=10.7 StartZ=0 EndX=17 EndY=14.7 EndZ=0
    g8: ArcOfCircle CenterX=7 CenterY=13.7 CenterZ=0 NormalX=0 NormalY=0 NormalZ=1 AngleXU=0 Radius=1 StartAngle=1.5708 EndAngle=3.14159
    g9: LineSegment StartX=25 StartY=10.7 StartZ=0 EndX=25 EndY=11.7 EndZ=0
    g10: ArcOfCircle CenterX=22 CenterY=11.7 CenterZ=0 NormalX=0 NormalY=0 NormalZ=1 AngleXU=0 Radius=3 StartAngle=3e-16 EndAngle=1.5708
    g11: LineSegment StartX=25 StartY=10.7 StartZ=0 EndX=34 EndY=10.7 EndZ=0
  constraints (30):
    c: Coincident(g0,g-3)
    c: Vertical(g0)
    c: Distance(g0) = 17
    c: Coincident(g1,g0)
    c: Horizontal(g1)
    c: Coincident(g2,g-6)
    c: Vertical(g2)
    c: Coincident(g1,g2)
    c: Coincident(g3,g-4)
    c: Horizontal(g3)
    c: Distance(g3) = 11
    c: Coincident(g4,g0)
    c: Coincident(g4,g3)
    c: Coincident(g5,g3)
    c: Vertical(g5)
    c: Horizontal(g6)
    c: Coincident(g7,g3)
    c: PointOnObject(g7,g6)
    c: Vertical(g7)
    c: Distance(g7) = 4
    c: Diameter(g8) = 2
    c: Tangent(g8,g6) = 1.5708
    c: Tangent(g8,g5) = 1.5708
    c: Coincident(g9,g-5)
    c: Vertical(g9)
    c: Tangent(g10,g9) = -1.5708
    c: Tangent(g10,g6) = 1.5708
    c: Diameter(g10) = 6
    c: Coincident(g11,g9)
    c: Coincident(g11,g2)
FEATURE [PartDesign::Pad] Pad005  label="Wall to Floor"
  BaseFeature = -> Pocket010
  Direction = (1,0,0)
  Length = 1.6
  Length2 = 10
  Profile = -> Sketch016
  ReferenceAxis = -> Sketch016 [N_Axis]
  Refine = true
  Reversed = true
  Suppressed = false
  Type = 0
  expr: Length = VarSet.WallThickness
FEATURE [Sketcher::SketchObject] Sketch017
  ArcFitTolerance = 1e-06
  AttachmentSupport = -> [Pad005]
  ExternalGeometry = -> [Pad005]
  FullyConstrained = true
  MakeInternals = false
  MapMode = 5
  Placement = pos=(50.4,0,0) rot=(0.57735,-0.57735,-0.57735;2.0944rad)
  sketch-geometry (4):
    g0: LineSegment StartX=-34 StartY=27.7 StartZ=0 EndX=34 EndY=27.7 EndZ=0
    g1: LineSegment StartX=-25 StartY=14.7 StartZ=0 EndX=25 EndY=14.7 EndZ=0
    g2: LineSegment StartX=-25 StartY=14.7 StartZ=0 EndX=-34 EndY=27.7 EndZ=0
    g3: LineSegment StartX=25 StartY=14.7 StartZ=0 EndX=34 EndY=27.7 EndZ=0
  constraints (10):
    c: Horizontal(g1)
    c: Coincident(g2,g-3)
    c: Coincident(g3,g1)
    c: Coincident(g3,g-3)
    c: Equal(g3,g2)
    c: PointOnObject(g-4,g1)
    c: Coincident(g0,g3)
    c: Coincident(g0,g2)
    c: Coincident(g2,g1)
    c: Distance(g1) = 50
FEATURE [PartDesign::Pad] Pad006  label="Floor Block"
  BaseFeature = -> Pad005
  Direction = (-1,0,0)
  Length = 9
  Length2 = 10
  Profile = -> Sketch017
  ReferenceAxis = -> Sketch017 [N_Axis]
  Refine = true
  Suppressed = false
  Type = 0
FEATURE [Sketcher::SketchObject] Sketch018
  ArcFitTolerance = 1e-06
  AttachmentSupport = -> [Pad006]
  ExternalGeometry = -> [Pad006]
  FullyConstrained = true
  MakeInternals = false
  MapMode = 5
  Placement = pos=(0,34,0) rot=(0,0.707107,0.707107;3.14159rad)
  sketch-geometry (3):
    g0: LineSegment StartX=-50.4 StartY=14.7 StartZ=0 EndX=-41.4 EndY=27.7 EndZ=0
    g1: LineSegment StartX=-41.4 StartY=27.7 StartZ=0 EndX=-41.4 EndY=14.7 EndZ=0
    g2: LineSegment StartX=-41.4 StartY=14.7 StartZ=0 EndX=-50.4 EndY=14.7 EndZ=0
  constraints (6):
    c: Coincident(g0,g-4)
    c: Coincident(g0,g-3)
    c: Coincident(g1,g-3)
    c: Coincident(g1,g-4)
    c: Coincident(g2,g-4)
    c: Coincident(g2,g-4)
FEATURE [PartDesign::Pocket] Pocket  label="Floor Rise"
  BaseFeature = -> Pad006
  Direction = (0,-1,2e-16)
  Length = 5
  Length2 = 5
  Profile = -> Sketch018
  ReferenceAxis = -> Sketch018 [N_Axis]
  Refine = true
  Suppressed = false
  Type = 1
FEATURE [Sketcher::SketchObject] Sketch019
  ArcFitTolerance = 1e-06
  AttachmentSupport = -> [Pocket]
  ExternalGeometry = -> [Pocket]
  FullyConstrained = true
  MakeInternals = false
  MapMode = 5
  Placement = pos=(0,0,27.7) rot=(0,0,1;0rad)
  sketch-geometry (10):
    g0: ArcOfCircle CenterX=41.4 CenterY=34 CenterZ=0 NormalX=0 NormalY=0 NormalZ=1 AngleXU=0 Radius=9 StartAngle=4.71239 EndAngle=6.28319
    g1: ArcOfCircle CenterX=41.4 CenterY=-34 CenterZ=0 NormalX=0 NormalY=0 NormalZ=1 AngleXU=0 Radius=9 StartAngle=0 EndAngle=1.5708
    g2: LineSegment StartX=41.4 StartY=-34 StartZ=0 EndX=41.4 EndY=-25 EndZ=0
    g3: LineSegment StartX=41.4 StartY=-34 StartZ=0 EndX=50.4 EndY=-34 EndZ=0
    g4: LineSegment StartX=41.4 StartY=34 StartZ=0 EndX=41.4 EndY=25 EndZ=0
    g5: LineSegment StartX=41.4 StartY=34 StartZ=0 EndX=50.4 EndY=34 EndZ=0
    g6: LineSegment StartX=41.4 StartY=-10.5 StartZ=0 EndX=41.4 EndY=10.5 EndZ=0
    g7: ArcOfCircle CenterX=41.4 CenterY=1.5 CenterZ=0 NormalX=0 NormalY=0 NormalZ=1 AngleXU=0 Radius=9 StartAngle=-9.95e-14 EndAngle=1.5708
    g8: LineSegment StartX=50.4 StartY=1.5 StartZ=0 EndX=50.4 EndY=-1.49998 EndZ=0
    g9: ArcOfCircle CenterX=41.4 CenterY=-1.5 CenterZ=0 NormalX=0 NormalY=0 NormalZ=1 AngleXU=0 Radius=9 StartAngle=4.71239 EndAngle=6.28319
  constraints (26):
    c: Coincident(g0,g-4)
    c: Coincident(g0,g-4)
    c: PointOnObject(g0,g-3)
    c: Coincident(g1,g-5)
    c: Coincident(g1,g-5)
    c: PointOnObject(g1,g-3)
    c: Coincident(g2,g1)
    c: Coincident(g2,g1)
    c: Coincident(g3,g1)
    c: Coincident(g3,g1)
    c: Coincident(g4,g0)
    c: Coincident(g4,g0)
    c: Coincident(g5,g0)
    c: Coincident(g5,g0)
    c: PointOnObject(g6,g-3)
    c: Symmetric(g6,g6,g-1)
    c: Distance(g6) = 21
    c: PointOnObject(g7,g6)
    c: Coincident(g7,g6)
    c: Equal(g7,g0)
    c: Vertical(g8)
    c: Tangent(g8,g7) = 1.5708
    c: PointOnObject(g9,g6)
    c: Coincident(g9,g6)
    c: Equal(g7,g9)
    c: Coincident(g9,g8)
FEATURE [PartDesign::Pocket] Pocket011  label="Screw Driver Access"
  BaseFeature = -> Pocket
  Direction = (0,0,-1)
  Length = 13
  Length2 = 5
  Profile = -> Sketch019
  ReferenceAxis = -> Sketch019 [N_Axis]
  Refine = true
  Suppressed = false
  Type = 0
FEATURE [Sketcher::SketchObject] Sketch020
  ArcFitTolerance = 1e-06
  AttachmentSupport = -> [Pocket011]
  ExternalGeometry = -> [Pocket011]
  FullyConstrained = true
  MakeInternals = false
  MapMode = 5
  Placement = pos=(0,0,27.7) rot=(0,0,1;0rad)
  expr: Constraints[4] = VarSet.BlackSelfTappingDiameter
  sketch-geometry (7):
    g0: Circle CenterX=46.7 CenterY=18 CenterZ=0 NormalX=0 NormalY=0 NormalZ=1 AngleXU=0 Radius=1.35
    g1: Circle CenterX=46.7 CenterY=-18 CenterZ=0 NormalX=0 NormalY=0 NormalZ=1 AngleXU=0 Radius=1.35
    g2: LineSegment [constr] StartX=46.7 StartY=18 StartZ=0 EndX=46.7 EndY=-18 EndZ=0
    g3: LineSegment [constr] StartX=46.7 StartY=18 StartZ=0 EndX=41.4 EndY=18 EndZ=0
    g4: LineSegment [constr] StartX=46.7 StartY=18 StartZ=0 EndX=52 EndY=18 EndZ=0
    g5: LineSegment [constr] StartX=46.7 StartY=18 StartZ=0 EndX=52 EndY=34 EndZ=0
    g6: LineSegment [constr] StartX=52 StartY=-34 StartZ=0 EndX=46.7 EndY=-18 EndZ=0
  constraints (18):
    c: Coincident(g2,g0)
    c: Vertical(g2)
    c: Coincident(g2,g1)
    c: Equal(g1,g0)
    c: Diameter(g1) = 2.7
    c: Coincident(g3,g0)
    c: Horizontal(g3)
    c: Coincident(g4,g0)
    c: PointOnObject(g4,g-3)
    c: Horizontal(g4)
    c: Equal(g4,g3)
    c: Distance(g2) = 36
    c: PointOnObject(g3,g-4)
    c: Coincident(g5,g0)
    c: Coincident(g5,g-3)
    c: Coincident(g6,g-3)
    c: Coincident(g6,g1)
    c: Equal(g5,g6)
FEATURE [PartDesign::Pocket] Pocket012  label="Floor Screws"
  BaseFeature = -> Pocket011
  Direction = (0,0,-1)
  Length = 5
  Length2 = 5
  Profile = -> Sketch020
  ReferenceAxis = -> Sketch020 [N_Axis]
  Refine = true
  Suppressed = false
  Type = 0
FEATURE [Sketcher::SketchObject] Sketch021
  ArcFitTolerance = 1e-06
  AttachmentSupport = -> [Pocket012]
  ExternalGeometry = -> [Pocket012]
  FullyConstrained = true
  MakeInternals = false
  MapMode = 5
  Placement = pos=(0,34,0) rot=(0,0.707107,0.707107;3.14159rad)
  sketch-geometry (3):
    g0: LineSegment StartX=-50.4 StartY=10.7 StartZ=0 EndX=-43.4 EndY=10.7 EndZ=0
    g1: LineSegment StartX=-50.4 StartY=10.7 StartZ=0 EndX=-50.4 EndY=17.7 EndZ=0
    g2: LineSegment StartX=-43.4 StartY=10.7 StartZ=0 EndX=-50.4 EndY=17.7 EndZ=0
  constraints (8):
    c: Coincident(g0,g-3)
    c: Horizontal(g0)
    c: Coincident(g1,g0)
    c: Vertical(g1)
    c: Coincident(g2,g0)
    c: Coincident(g2,g1)
    c: Equal(g0,g1)
    c: Distance(g0) = 7
FEATURE [PartDesign::Pad] Pad007  label="Wall to Body 1"
  BaseFeature = -> Pocket012
  Direction = (0,1,-2e-16)
  Length = 1.6
  Length2 = 10
  Profile = -> Sketch021
  ReferenceAxis = -> Sketch021 [N_Axis]
  Refine = true
  Reversed = true
  Suppressed = false
  Type = 0
  expr: Length = VarSet.WallThickness
FEATURE [Sketcher::SketchObject] Sketch022
  ArcFitTolerance = 1e-06
  AttachmentSupport = -> [Pad007]
  ExternalGeometry = -> [Pad007]
  FullyConstrained = true
  MakeInternals = false
  MapMode = 5
  Placement = pos=(-6.764e-13,-34,-3.288e-13) rot=(1,0,0;1.5708rad)
  sketch-geometry (3):
    g0: LineSegment StartX=50.4 StartY=10.7 StartZ=0 EndX=43.4 EndY=10.7 EndZ=0
    g1: LineSegment StartX=50.4 StartY=10.7 StartZ=0 EndX=50.4 EndY=17.7 EndZ=0
    g2: LineSegment StartX=43.4 StartY=10.7 StartZ=0 EndX=50.4 EndY=17.7 EndZ=0
  constraints (8):
    c: Coincident(g0,g-3)
    c: Horizontal(g0)
    c: Coincident(g1,g0)
    c: Vertical(g1)
    c: Coincident(g2,g0)
    c: Coincident(g2,g1)
    c: Equal(g0,g1)
    c: Distance(g0) = 7
FEATURE [PartDesign::Pad] Pad008  label="Wall to Body 2"
  BaseFeature = -> Pad007
  Direction = (-1.99e-14,-1,-9.5e-15)
  Length = 1.6
  Length2 = 10
  Profile = -> Sketch022
  ReferenceAxis = -> Sketch022 [N_Axis]
  Refine = true
  Reversed = true
  Suppressed = false
  Type = 0
  expr: Length = VarSet.WallThickness
FEATURE [Sketcher::SketchObject] Sketch023
  ArcFitTolerance = 1e-06
  AttachmentSupport = -> [Pad008]
  ExternalGeometry = -> [Pad008]
  FullyConstrained = true
  MakeInternals = false
  MapMode = 5
  Placement = pos=(52,1.0692e-12,-4.0489e-12) rot=(0.57735,0.57735,0.57735;2.0944rad)
  sketch-geometry (4):
    g0: LineSegment StartX=-8 StartY=27.7 StartZ=0 EndX=8 EndY=27.7 EndZ=0
    g1: LineSegment StartX=4 StartY=23.7 StartZ=0 EndX=-3.99997 EndY=23.7 EndZ=0
    g2: ArcOfCircle CenterX=4 CenterY=27.7 CenterZ=0 NormalX=0 NormalY=0 NormalZ=1 AngleXU=0 Radius=4 StartAngle=4.71239 EndAngle=6.28319
    g3: ArcOfCircle CenterX=-4 CenterY=27.7 CenterZ=0 NormalX=0 NormalY=0 NormalZ=1 AngleXU=0 Radius=4 StartAngle=3.14159 EndAngle=4.7124
  constraints (12):
    c: PointOnObject(g0,g-3)
    c: Symmetric(g0,g0,g-2)
    c: Distance(g0) = 16
    c: Horizontal(g1)
    c: PointOnObject(g2,g0)
    c: Coincident(g2,g0)
    c: Diameter(g2) = 8
    c: Tangent(g2,g1) = 1.5708
    c: PointOnObject(g3,g0)
    c: Coincident(g3,g0)
    c: Equal(g3,g2)
    c: Coincident(g3,g1)
FEATURE [PartDesign::Pocket] Pocket013  label="RS232 Passage"
  BaseFeature = -> Pad008
  Direction = (-1,-2.04e-14,7.77e-14)
  Length = 5
  Length2 = 5
  Profile = -> Sketch023
  ReferenceAxis = -> Sketch023 [N_Axis]
  Refine = true
  Suppressed = false
  Type = 0
FEATURE [PartDesign::Body] Body
  AllowCompound = false
  Group = -> [Sketch,Pad,Sketch002,Pad001,Sketch003,Pad002,Pad004,Sketch004,Pad003,Sketch005,Pocket001,Sketch006,Pocket002,Sketch007,Pocket003,Sketch008,Pocket004,Sketch009,Pocket005,Sketch010,Pocket006,Sketch012,Pocket008,Sketch013,Pocket009,Sketch014,Pocket010,Sketch015,Sketch016,Pad005,Sketch017,Pad006,Sketch018,Pocket,Sketch019,Pocket011,Sketch020,Pocket012,Sketch021,Pad007,Sketch022,Pad008,Sketch023,+1 more]
  Origin = -> Origin
  Tip = -> Pocket013
